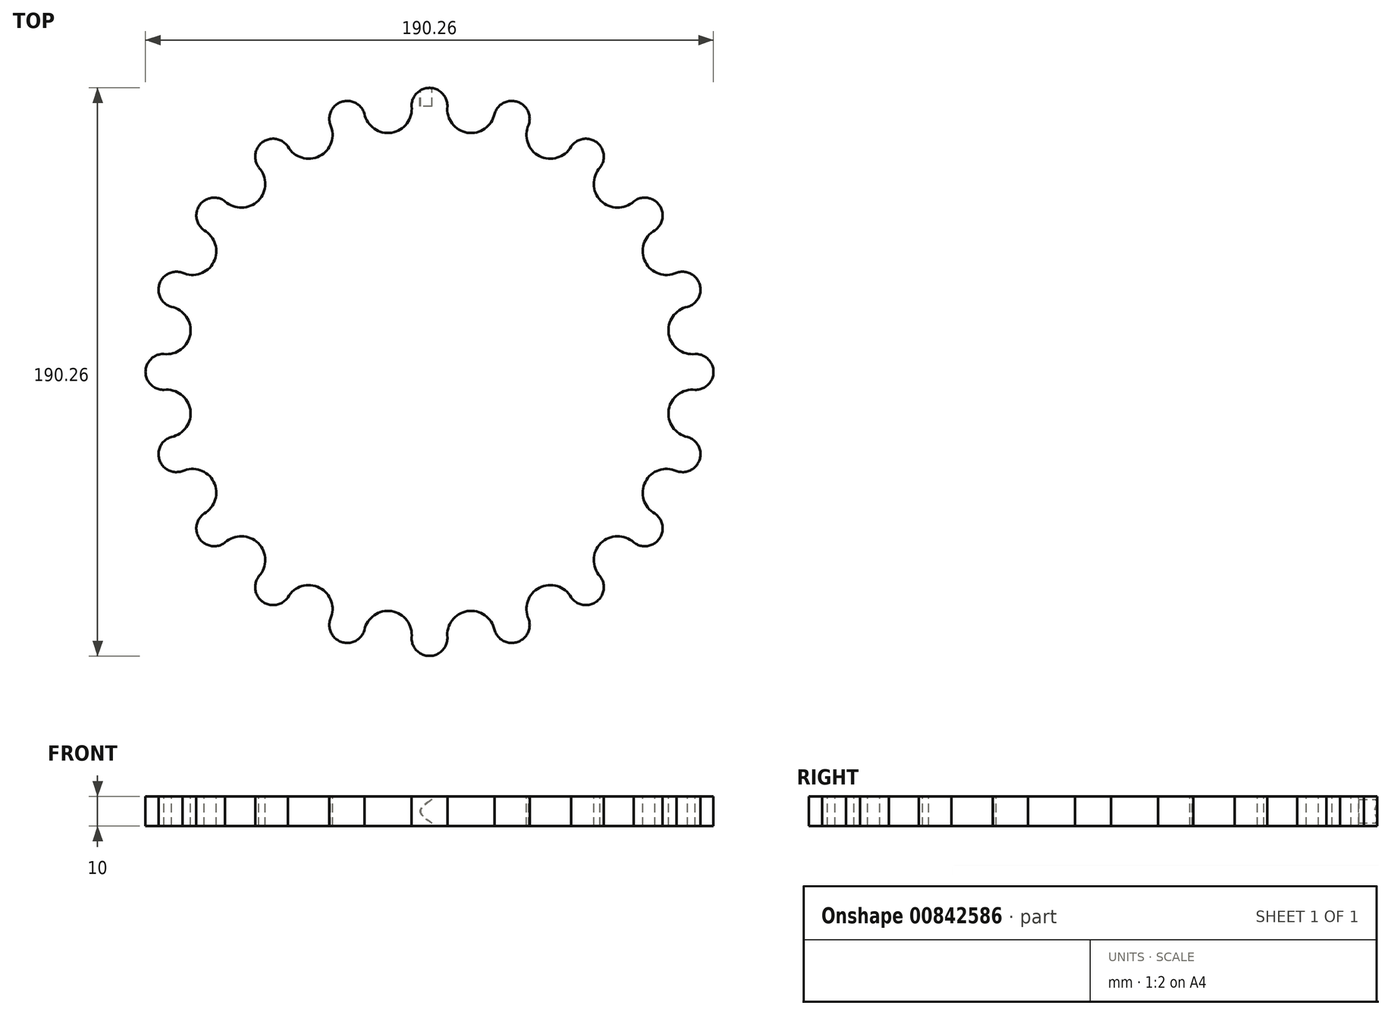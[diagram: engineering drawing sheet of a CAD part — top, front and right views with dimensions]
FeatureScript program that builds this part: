
annotation { "Feature Type Name" : "Feature", "Feature Type Description" : "" }
export const myFeature = defineFeature(function(context is Context, id is Id, definition is map)
    precondition{}
    {
        {
            var Q0;
            Q0=qCreatedBy(makeId("Top.planeOp"),FACE);
            var sketch = newSketch(context, id + "F0", { "sketchPlane" : qUnion([Q0])});
            skCircle(sketch, "E0", {"center": v(0, 0) * mm, "radius": 89.13 * mm});
            skCircle(sketch, "E1", {"center": v(0, 89.13) * mm, "radius": 7 * mm});
            skCircle(sketch, "E2.1.0", {"center": v(-13.94, 88.03) * mm, "radius": 7 * mm});
            skCircle(sketch, "E2.2.0", {"center": v(-27.54, 84.76) * mm, "radius": 7 * mm});
            skCircle(sketch, "E2.3.0", {"center": v(-40.46, 79.41) * mm, "radius": 7 * mm});
            skCircle(sketch, "E2.4.0", {"center": v(-52.39, 72.1) * mm, "radius": 7 * mm});
            skCircle(sketch, "E2.5.0", {"center": v(-63.02, 63.02) * mm, "radius": 7 * mm});
            skCircle(sketch, "E2.6.0", {"center": v(-72.1, 52.39) * mm, "radius": 7 * mm});
            skCircle(sketch, "E2.7.0", {"center": v(-79.41, 40.46) * mm, "radius": 7 * mm});
            skCircle(sketch, "E2.8.0", {"center": v(-84.76, 27.54) * mm, "radius": 7 * mm});
            skCircle(sketch, "E2.9.0", {"center": v(-88.03, 13.94) * mm, "radius": 7 * mm});
            skCircle(sketch, "E2.10.0", {"center": v(-89.13, 0) * mm, "radius": 7 * mm});
            skCircle(sketch, "E2.11.0", {"center": v(-88.03, -13.94) * mm, "radius": 7 * mm});
            skCircle(sketch, "E2.12.0", {"center": v(-84.76, -27.54) * mm, "radius": 7 * mm});
            skCircle(sketch, "E2.13.0", {"center": v(-79.41, -40.46) * mm, "radius": 7 * mm});
            skCircle(sketch, "E2.14.0", {"center": v(-72.1, -52.39) * mm, "radius": 7 * mm});
            skCircle(sketch, "E2.15.0", {"center": v(-63.02, -63.02) * mm, "radius": 7 * mm});
            skCircle(sketch, "E2.16.0", {"center": v(-52.39, -72.1) * mm, "radius": 7 * mm});
            skCircle(sketch, "E2.17.0", {"center": v(-40.46, -79.41) * mm, "radius": 7 * mm});
            skCircle(sketch, "E2.18.0", {"center": v(-27.54, -84.76) * mm, "radius": 7 * mm});
            skCircle(sketch, "E2.19.0", {"center": v(-13.94, -88.03) * mm, "radius": 7 * mm});
            skCircle(sketch, "E2.20.0", {"center": v(0, -89.13) * mm, "radius": 7 * mm});
            skCircle(sketch, "E2.21.0", {"center": v(13.94, -88.03) * mm, "radius": 7 * mm});
            skCircle(sketch, "E2.22.0", {"center": v(27.54, -84.76) * mm, "radius": 7 * mm});
            skCircle(sketch, "E2.23.0", {"center": v(40.46, -79.41) * mm, "radius": 7 * mm});
            skCircle(sketch, "E2.24.0", {"center": v(52.39, -72.1) * mm, "radius": 7 * mm});
            skCircle(sketch, "E2.25.0", {"center": v(63.02, -63.02) * mm, "radius": 7 * mm});
            skCircle(sketch, "E2.26.0", {"center": v(72.1, -52.39) * mm, "radius": 7 * mm});
            skCircle(sketch, "E2.27.0", {"center": v(79.41, -40.46) * mm, "radius": 7 * mm});
            skCircle(sketch, "E2.28.0", {"center": v(84.76, -27.54) * mm, "radius": 7 * mm});
            skCircle(sketch, "E2.29.0", {"center": v(88.03, -13.94) * mm, "radius": 7 * mm});
            skCircle(sketch, "E2.30.0", {"center": v(89.13, 0) * mm, "radius": 7 * mm});
            skCircle(sketch, "E2.31.0", {"center": v(88.03, 13.94) * mm, "radius": 7 * mm});
            skCircle(sketch, "E2.32.0", {"center": v(84.76, 27.54) * mm, "radius": 7 * mm});
            skCircle(sketch, "E2.33.0", {"center": v(79.41, 40.46) * mm, "radius": 7 * mm});
            skCircle(sketch, "E2.34.0", {"center": v(72.1, 52.39) * mm, "radius": 7 * mm});
            skCircle(sketch, "E2.35.0", {"center": v(63.02, 63.02) * mm, "radius": 7 * mm});
            skCircle(sketch, "E2.36.0", {"center": v(52.39, 72.1) * mm, "radius": 7 * mm});
            skCircle(sketch, "E2.37.0", {"center": v(40.46, 79.41) * mm, "radius": 7 * mm});
            skCircle(sketch, "E2.38.0", {"center": v(27.54, 84.76) * mm, "radius": 7 * mm});
            skCircle(sketch, "E2.39.0", {"center": v(13.94, 88.03) * mm, "radius": 7 * mm});
            skSolve(sketch);
        }
        {
            var Q0;
            {var subQ32=sQuery(id+"F0.wireOp",EDGE,"E2.1.0");var subQ34=sQuery(id+"F0.wireOp",EDGE,"E1");var subQ35=makeQuery(id+"F0.imprint","INTERSECT",VERTEX,{"disambiguationData":[OD(1.0)],"derivedFrom":[subQ34,subQ32]});Q0=makeQuery(id+"F0.imprint","IMPRINT",FACE,{"disambiguationData":[TD([[makeQuery(id+"F0.imprint","IMPRINT",EDGE,{"disambiguationData":[TD([[subQ35,-1.0]])],"derivedFrom":subQ34}),-1.0]])]});}
            var sketch = newSketch(context, id + "F1", { "sketchPlane" : qUnion([Q0])});
            skArc(sketch, "E3.0", {"start": v(-67.8, 57.91) * mm, "mid": v(-58.07, 58.07) * mm, "end": v(-57.91, 67.8) * mm});
            skArc(sketch, "E4.0.0", {"start": v(-57.91, 67.8) * mm, "mid": v(-57.9, 67.79) * mm, "end": v(-57.88, 67.77) * mm});
            skArc(sketch, "E4.0.2", {"start": v(-46.26, 75.49) * mm, "mid": v(-46.43, 75.76) * mm, "end": v(-46.6, 76.03) * mm});
            skArc(sketch, "E4.0.3", {"start": v(-46.6, 76.03) * mm, "mid": v(-56.5, 77.77) * mm, "end": v(-57.91, 67.8) * mm});
            skArc(sketch, "E5.0.0", {"start": v(-7, 88.85) * mm, "mid": v(-12.85, 81.12) * mm, "end": v(-20.8, 86.66) * mm});
            skArc(sketch, "E5.0.2", {"start": v(-34.1, 82.34) * mm, "mid": v(-37.02, 73.32) * mm, "end": v(-46.26, 75.49) * mm});
            skArc(sketch, "E5.0.4", {"start": v(-57.5, 67.32) * mm, "mid": v(-58.07, 58.07) * mm, "end": v(-67.32, 57.5) * mm});
            skArc(sketch, "E5.0.6", {"start": v(-75.49, 46.26) * mm, "mid": v(-73.32, 37.02) * mm, "end": v(-82.34, 34.1) * mm});
            skArc(sketch, "E5.0.8", {"start": v(-86.09, 20.67) * mm, "mid": v(-81.17, 12.56) * mm, "end": v(-88.85, 7) * mm});
            skArc(sketch, "E5.0.10", {"start": v(-88.85, -7) * mm, "mid": v(-81.12, -12.85) * mm, "end": v(-86.66, -20.8) * mm});
            skArc(sketch, "E5.0.12", {"start": v(-82.34, -34.1) * mm, "mid": v(-73.17, -37.3) * mm, "end": v(-76.03, -46.6) * mm});
            skArc(sketch, "E5.0.14", {"start": v(-67.77, -57.88) * mm, "mid": v(-58.07, -58.07) * mm, "end": v(-57.88, -67.77) * mm});
            skArc(sketch, "E5.0.16", {"start": v(-46.57, -76) * mm, "mid": v(-37.28, -73.18) * mm, "end": v(-34.1, -82.34) * mm});
            skArc(sketch, "E5.0.18", {"start": v(-20.8, -86.66) * mm, "mid": v(-12.85, -81.12) * mm, "end": v(-7, -88.85) * mm});
            skArc(sketch, "E5.0.20", {"start": v(7, -88.85) * mm, "mid": v(12.85, -81.12) * mm, "end": v(20.8, -86.66) * mm});
            skArc(sketch, "E5.0.22", {"start": v(34.12, -82.38) * mm, "mid": v(37.28, -73.18) * mm, "end": v(46.6, -76.03) * mm});
            skArc(sketch, "E5.0.24", {"start": v(57.88, -67.77) * mm, "mid": v(58.07, -58.07) * mm, "end": v(67.77, -57.88) * mm});
            skArc(sketch, "E5.0.26", {"start": v(76, -46.57) * mm, "mid": v(73.18, -37.28) * mm, "end": v(82.34, -34.1) * mm});
            skArc(sketch, "E5.0.28", {"start": v(86.66, -20.8) * mm, "mid": v(81.12, -12.85) * mm, "end": v(88.85, -7) * mm});
            skArc(sketch, "E5.0.30", {"start": v(88.85, 7) * mm, "mid": v(81.12, 12.85) * mm, "end": v(86.66, 20.8) * mm});
            skArc(sketch, "E5.0.32", {"start": v(82.34, 34.1) * mm, "mid": v(73.18, 37.28) * mm, "end": v(76, 46.57) * mm});
            skArc(sketch, "E5.0.34", {"start": v(67.77, 57.88) * mm, "mid": v(58.07, 58.07) * mm, "end": v(57.88, 67.77) * mm});
            skArc(sketch, "E5.0.36", {"start": v(46.57, 76) * mm, "mid": v(37.28, 73.18) * mm, "end": v(34.1, 82.34) * mm});
            skArc(sketch, "E5.0.38", {"start": v(20.8, 86.66) * mm, "mid": v(12.85, 81.12) * mm, "end": v(7, 88.85) * mm});
            skArc(sketch, "E6.0.0", {"start": v(-34.12, 82.38) * mm, "mid": v(-34.11, 82.36) * mm, "end": v(-34.1, 82.34) * mm});
            skArc(sketch, "E6.0.2", {"start": v(-20.8, 86.66) * mm, "mid": v(-20.81, 86.68) * mm, "end": v(-20.82, 86.7) * mm});
            skArc(sketch, "E6.0.3", {"start": v(-20.82, 86.7) * mm, "mid": v(-29.7, 91.42) * mm, "end": v(-34.12, 82.38) * mm});
            skArc(sketch, "E7.0.0", {"start": v(-7, 88.9) * mm, "mid": v(-7, 88.87) * mm, "end": v(-7, 88.85) * mm});
            skArc(sketch, "E7.0.2", {"start": v(7, 88.85) * mm, "mid": v(7, 88.87) * mm, "end": v(7, 88.9) * mm});
            skArc(sketch, "E7.0.3", {"start": v(7, 88.9) * mm, "mid": v(0, 96.13) * mm, "end": v(-7, 88.9) * mm});
            skArc(sketch, "E8.0.0", {"start": v(20.82, 86.7) * mm, "mid": v(20.81, 86.68) * mm, "end": v(20.8, 86.66) * mm});
            skArc(sketch, "E8.0.2", {"start": v(34.1, 82.34) * mm, "mid": v(34.11, 82.36) * mm, "end": v(34.12, 82.38) * mm});
            skArc(sketch, "E8.0.3", {"start": v(34.12, 82.38) * mm, "mid": v(29.7, 91.42) * mm, "end": v(20.82, 86.7) * mm});
            skArc(sketch, "E9.0.0", {"start": v(46.6, 76.03) * mm, "mid": v(46.58, 76.01) * mm, "end": v(46.57, 76) * mm});
            skArc(sketch, "E9.0.2", {"start": v(57.88, 67.77) * mm, "mid": v(57.9, 67.79) * mm, "end": v(57.91, 67.8) * mm});
            skArc(sketch, "E9.0.3", {"start": v(57.91, 67.8) * mm, "mid": v(56.5, 77.77) * mm, "end": v(46.6, 76.03) * mm});
            skArc(sketch, "E10.0.0", {"start": v(67.8, 57.91) * mm, "mid": v(67.79, 57.9) * mm, "end": v(67.77, 57.88) * mm});
            skArc(sketch, "E10.0.2", {"start": v(76, 46.57) * mm, "mid": v(76.01, 46.58) * mm, "end": v(76.03, 46.6) * mm});
            skArc(sketch, "E10.0.3", {"start": v(76.03, 46.6) * mm, "mid": v(77.77, 56.5) * mm, "end": v(67.8, 57.91) * mm});
            skArc(sketch, "E11.0.0", {"start": v(82.38, 34.12) * mm, "mid": v(82.36, 34.11) * mm, "end": v(82.34, 34.1) * mm});
            skArc(sketch, "E11.0.2", {"start": v(86.66, 20.8) * mm, "mid": v(86.68, 20.81) * mm, "end": v(86.7, 20.82) * mm});
            skArc(sketch, "E11.0.3", {"start": v(86.7, 20.82) * mm, "mid": v(91.42, 29.7) * mm, "end": v(82.38, 34.12) * mm});
            skArc(sketch, "E12.0.0", {"start": v(88.85, -7) * mm, "mid": v(88.87, -7) * mm, "end": v(88.9, -7) * mm});
            skArc(sketch, "E12.0.1", {"start": v(88.9, -7) * mm, "mid": v(96.13, 0) * mm, "end": v(88.9, 7) * mm});
            skArc(sketch, "E12.0.2", {"start": v(88.9, 7) * mm, "mid": v(88.87, 7) * mm, "end": v(88.85, 7) * mm});
            skArc(sketch, "E13.0.0", {"start": v(86.7, -20.82) * mm, "mid": v(86.68, -20.81) * mm, "end": v(86.66, -20.8) * mm});
            skArc(sketch, "E13.0.2", {"start": v(82.34, -34.1) * mm, "mid": v(82.36, -34.11) * mm, "end": v(82.38, -34.12) * mm});
            skArc(sketch, "E13.0.3", {"start": v(82.38, -34.12) * mm, "mid": v(91.42, -29.7) * mm, "end": v(86.7, -20.82) * mm});
            skArc(sketch, "E14.0.0", {"start": v(76.03, -46.6) * mm, "mid": v(76.01, -46.58) * mm, "end": v(76, -46.57) * mm});
            skArc(sketch, "E14.0.2", {"start": v(67.77, -57.88) * mm, "mid": v(67.79, -57.9) * mm, "end": v(67.8, -57.91) * mm});
            skArc(sketch, "E14.0.3", {"start": v(67.8, -57.91) * mm, "mid": v(77.77, -56.5) * mm, "end": v(76.03, -46.6) * mm});
            skArc(sketch, "E15.0.0", {"start": v(57.91, -67.8) * mm, "mid": v(57.9, -67.79) * mm, "end": v(57.88, -67.77) * mm});
            skArc(sketch, "E15.0.2", {"start": v(46.57, -76) * mm, "mid": v(46.58, -76.01) * mm, "end": v(46.6, -76.03) * mm});
            skArc(sketch, "E15.0.3", {"start": v(46.6, -76.03) * mm, "mid": v(56.5, -77.77) * mm, "end": v(57.91, -67.8) * mm});
            skArc(sketch, "E16.0.0", {"start": v(34.12, -82.38) * mm, "mid": v(34.11, -82.36) * mm, "end": v(34.1, -82.34) * mm});
            skArc(sketch, "E16.0.2", {"start": v(20.8, -86.66) * mm, "mid": v(20.81, -86.68) * mm, "end": v(20.82, -86.7) * mm});
            skArc(sketch, "E16.0.3", {"start": v(20.82, -86.7) * mm, "mid": v(29.7, -91.42) * mm, "end": v(34.12, -82.38) * mm});
            skArc(sketch, "E17.0.0", {"start": v(7, -88.9) * mm, "mid": v(7, -88.87) * mm, "end": v(7, -88.85) * mm});
            skArc(sketch, "E17.0.2", {"start": v(-7, -88.85) * mm, "mid": v(-7, -88.87) * mm, "end": v(-7, -88.9) * mm});
            skArc(sketch, "E17.0.3", {"start": v(-7, -88.9) * mm, "mid": v(0, -96.13) * mm, "end": v(7, -88.9) * mm});
            skArc(sketch, "E18.0.0", {"start": v(-20.82, -86.7) * mm, "mid": v(-20.81, -86.68) * mm, "end": v(-20.8, -86.66) * mm});
            skArc(sketch, "E18.0.2", {"start": v(-34.1, -82.34) * mm, "mid": v(-34.11, -82.36) * mm, "end": v(-34.12, -82.38) * mm});
            skArc(sketch, "E18.0.3", {"start": v(-34.12, -82.38) * mm, "mid": v(-29.7, -91.42) * mm, "end": v(-20.82, -86.7) * mm});
            skArc(sketch, "E19.0.0", {"start": v(-46.6, -76.03) * mm, "mid": v(-46.58, -76.01) * mm, "end": v(-46.57, -76) * mm});
            skArc(sketch, "E19.0.2", {"start": v(-57.88, -67.77) * mm, "mid": v(-57.9, -67.79) * mm, "end": v(-57.91, -67.8) * mm});
            skArc(sketch, "E19.0.3", {"start": v(-57.91, -67.8) * mm, "mid": v(-56.5, -77.77) * mm, "end": v(-46.6, -76.03) * mm});
            skArc(sketch, "E20.0.0", {"start": v(-67.8, -57.91) * mm, "mid": v(-67.79, -57.9) * mm, "end": v(-67.77, -57.88) * mm});
            skArc(sketch, "E20.0.2", {"start": v(-76, -46.57) * mm, "mid": v(-76.01, -46.58) * mm, "end": v(-76.03, -46.6) * mm});
            skArc(sketch, "E20.0.3", {"start": v(-76.03, -46.6) * mm, "mid": v(-77.77, -56.5) * mm, "end": v(-67.8, -57.91) * mm});
            skArc(sketch, "E21.0.0", {"start": v(-82.38, -34.12) * mm, "mid": v(-82.36, -34.11) * mm, "end": v(-82.34, -34.1) * mm});
            skArc(sketch, "E21.0.2", {"start": v(-86.66, -20.8) * mm, "mid": v(-86.68, -20.81) * mm, "end": v(-86.7, -20.82) * mm});
            skArc(sketch, "E21.0.3", {"start": v(-86.7, -20.82) * mm, "mid": v(-91.42, -29.7) * mm, "end": v(-82.38, -34.12) * mm});
            skArc(sketch, "E22.0.0", {"start": v(-88.9, -7) * mm, "mid": v(-88.87, -7) * mm, "end": v(-88.85, -7) * mm});
            skArc(sketch, "E22.0.2", {"start": v(-88.85, 7) * mm, "mid": v(-88.87, 7) * mm, "end": v(-88.9, 7) * mm});
            skArc(sketch, "E22.0.3", {"start": v(-88.9, 7) * mm, "mid": v(-96.13, 0) * mm, "end": v(-88.9, -7) * mm});
            skArc(sketch, "E23.0.0", {"start": v(-86.7, 20.82) * mm, "mid": v(-86.4, 20.75) * mm, "end": v(-86.09, 20.67) * mm});
            skArc(sketch, "E23.0.2", {"start": v(-82.34, 34.1) * mm, "mid": v(-82.36, 34.11) * mm, "end": v(-82.38, 34.12) * mm});
            skArc(sketch, "E23.0.3", {"start": v(-82.38, 34.12) * mm, "mid": v(-91.42, 29.7) * mm, "end": v(-86.7, 20.82) * mm});
            skArc(sketch, "E24.0.0", {"start": v(-76.03, 46.6) * mm, "mid": v(-75.76, 46.43) * mm, "end": v(-75.49, 46.26) * mm});
            skArc(sketch, "E24.0.2", {"start": v(-67.77, 57.88) * mm, "mid": v(-67.79, 57.9) * mm, "end": v(-67.8, 57.91) * mm});
            skArc(sketch, "E24.0.3", {"start": v(-67.8, 57.91) * mm, "mid": v(-77.77, 56.5) * mm, "end": v(-76.03, 46.6) * mm});
            skPoint(sketch, "E25.orphan", {"position": v(-86.66, 20.8) * mm});
            skPoint(sketch, "E26.orphan", {"position": v(-81.8, 33.88) * mm});
            skPoint(sketch, "E27.orphan", {"position": v(-76, 46.57) * mm});
            skPoint(sketch, "E28.orphan", {"position": v(-46.57, 76) * mm});
            skPoint(sketch, "E29.orphan", {"position": v(-33.88, 81.8) * mm});
            skPoint(sketch, "E30.orphan", {"position": v(-20.67, 86.09) * mm});
            skPoint(sketch, "E31.orphan", {"position": v(-6.95, 88.26) * mm});
            skPoint(sketch, "E32.orphan", {"position": v(6.95, 88.26) * mm});
            skPoint(sketch, "E33.orphan", {"position": v(20.67, 86.09) * mm});
            skPoint(sketch, "E34.orphan", {"position": v(33.88, 81.8) * mm});
            skPoint(sketch, "E35.orphan", {"position": v(46.26, 75.49) * mm});
            skPoint(sketch, "E36.orphan", {"position": v(57.5, 67.32) * mm});
            skPoint(sketch, "E37.orphan", {"position": v(67.32, 57.5) * mm});
            skPoint(sketch, "E38.orphan", {"position": v(75.49, 46.26) * mm});
            skPoint(sketch, "E39.orphan", {"position": v(81.8, 33.88) * mm});
            skPoint(sketch, "E40.orphan", {"position": v(86.09, 20.67) * mm});
            skPoint(sketch, "E41.orphan", {"position": v(88.26, 6.95) * mm});
            skPoint(sketch, "E42.orphan", {"position": v(88.26, -6.95) * mm});
            skPoint(sketch, "E43.orphan", {"position": v(86.09, -20.67) * mm});
            skPoint(sketch, "E44.orphan", {"position": v(81.8, -33.88) * mm});
            skPoint(sketch, "E45.orphan", {"position": v(75.49, -46.26) * mm});
            skPoint(sketch, "E46.orphan", {"position": v(67.32, -57.5) * mm});
            skPoint(sketch, "E47.orphan", {"position": v(57.5, -67.32) * mm});
            skPoint(sketch, "E48.orphan", {"position": v(46.26, -75.49) * mm});
            skPoint(sketch, "E49.orphan", {"position": v(33.88, -81.8) * mm});
            skPoint(sketch, "E50.orphan", {"position": v(20.67, -86.09) * mm});
            skPoint(sketch, "E51.orphan", {"position": v(6.95, -88.26) * mm});
            skPoint(sketch, "E52.orphan", {"position": v(-6.95, -88.26) * mm});
            skPoint(sketch, "E53.orphan", {"position": v(-20.67, -86.09) * mm});
            skPoint(sketch, "E54.orphan", {"position": v(-33.88, -81.8) * mm});
            skPoint(sketch, "E55.orphan", {"position": v(-46.26, -75.49) * mm});
            skPoint(sketch, "E56.orphan", {"position": v(-57.5, -67.32) * mm});
            skPoint(sketch, "E57.orphan", {"position": v(-67.32, -57.5) * mm});
            skPoint(sketch, "E58.orphan", {"position": v(-75.49, -46.26) * mm});
            skPoint(sketch, "E59.orphan", {"position": v(-81.8, -33.88) * mm});
            skPoint(sketch, "E60.orphan", {"position": v(-86.09, -20.67) * mm});
            skPoint(sketch, "E61.orphan", {"position": v(-88.26, -6.95) * mm});
            skPoint(sketch, "E62.orphan", {"position": v(-88.26, 6.95) * mm});
            skSolve(sketch);
        }
        {
            var Q0;
            Q0 = qSketchRegion(id + "F1", true);
            extrude(context, id + "F2", {"entities" : qUnion([Q0]), "depth" : 10 * mm, "offsetDistance" : 25 * mm});
        }
        {
            var Q0;
            Q0=makeQuery(id+"F2.opExtrude","CAP_FACE",FACE,{"disambiguationData":[OSD([sQuery(id+"F1.wireOp",EDGE,"E3.0"),sQuery(id+"F1.wireOp",EDGE,"E4.0.0"),sQuery(id+"F1.wireOp",EDGE,"E4.0.2"),sQuery(id+"F1.wireOp",EDGE,"E4.0.3"),sQuery(id+"F1.wireOp",EDGE,"E5.0.0"),sQuery(id+"F1.wireOp",EDGE,"E5.0.2"),sQuery(id+"F1.wireOp",EDGE,"E5.0.4"),sQuery(id+"F1.wireOp",EDGE,"E5.0.6"),sQuery(id+"F1.wireOp",EDGE,"E5.0.8"),sQuery(id+"F1.wireOp",EDGE,"E5.0.10"),sQuery(id+"F1.wireOp",EDGE,"E5.0.12"),sQuery(id+"F1.wireOp",EDGE,"E5.0.14"),sQuery(id+"F1.wireOp",EDGE,"E5.0.16"),sQuery(id+"F1.wireOp",EDGE,"E5.0.18"),sQuery(id+"F1.wireOp",EDGE,"E5.0.20"),sQuery(id+"F1.wireOp",EDGE,"E5.0.22"),sQuery(id+"F1.wireOp",EDGE,"E5.0.24"),sQuery(id+"F1.wireOp",EDGE,"E5.0.26"),sQuery(id+"F1.wireOp",EDGE,"E5.0.28"),sQuery(id+"F1.wireOp",EDGE,"E5.0.30"),sQuery(id+"F1.wireOp",EDGE,"E5.0.32"),sQuery(id+"F1.wireOp",EDGE,"E5.0.34"),sQuery(id+"F1.wireOp",EDGE,"E5.0.36"),sQuery(id+"F1.wireOp",EDGE,"E5.0.38"),sQuery(id+"F1.wireOp",EDGE,"E6.0.0"),sQuery(id+"F1.wireOp",EDGE,"E6.0.2"),sQuery(id+"F1.wireOp",EDGE,"E6.0.3"),sQuery(id+"F1.wireOp",EDGE,"E7.0.0"),sQuery(id+"F1.wireOp",EDGE,"E7.0.2"),sQuery(id+"F1.wireOp",EDGE,"E7.0.3"),sQuery(id+"F1.wireOp",EDGE,"E8.0.0"),sQuery(id+"F1.wireOp",EDGE,"E8.0.2"),sQuery(id+"F1.wireOp",EDGE,"E8.0.3"),sQuery(id+"F1.wireOp",EDGE,"E9.0.0"),sQuery(id+"F1.wireOp",EDGE,"E9.0.2"),sQuery(id+"F1.wireOp",EDGE,"E9.0.3"),sQuery(id+"F1.wireOp",EDGE,"E10.0.0"),sQuery(id+"F1.wireOp",EDGE,"E10.0.2"),sQuery(id+"F1.wireOp",EDGE,"E10.0.3"),sQuery(id+"F1.wireOp",EDGE,"E11.0.0"),sQuery(id+"F1.wireOp",EDGE,"E11.0.2"),sQuery(id+"F1.wireOp",EDGE,"E11.0.3"),sQuery(id+"F1.wireOp",EDGE,"E12.0.0"),sQuery(id+"F1.wireOp",EDGE,"E12.0.1"),sQuery(id+"F1.wireOp",EDGE,"E12.0.2"),sQuery(id+"F1.wireOp",EDGE,"E13.0.0"),sQuery(id+"F1.wireOp",EDGE,"E13.0.2"),sQuery(id+"F1.wireOp",EDGE,"E13.0.3"),sQuery(id+"F1.wireOp",EDGE,"E14.0.0"),sQuery(id+"F1.wireOp",EDGE,"E14.0.2"),sQuery(id+"F1.wireOp",EDGE,"E14.0.3"),sQuery(id+"F1.wireOp",EDGE,"E15.0.0"),sQuery(id+"F1.wireOp",EDGE,"E15.0.2"),sQuery(id+"F1.wireOp",EDGE,"E15.0.3"),sQuery(id+"F1.wireOp",EDGE,"E16.0.0"),sQuery(id+"F1.wireOp",EDGE,"E16.0.2"),sQuery(id+"F1.wireOp",EDGE,"E16.0.3"),sQuery(id+"F1.wireOp",EDGE,"E17.0.0"),sQuery(id+"F1.wireOp",EDGE,"E17.0.2"),sQuery(id+"F1.wireOp",EDGE,"E17.0.3"),sQuery(id+"F1.wireOp",EDGE,"E18.0.0"),sQuery(id+"F1.wireOp",EDGE,"E18.0.2"),sQuery(id+"F1.wireOp",EDGE,"E18.0.3"),sQuery(id+"F1.wireOp",EDGE,"E19.0.0"),sQuery(id+"F1.wireOp",EDGE,"E19.0.2"),sQuery(id+"F1.wireOp",EDGE,"E19.0.3"),sQuery(id+"F1.wireOp",EDGE,"E20.0.0"),sQuery(id+"F1.wireOp",EDGE,"E20.0.2"),sQuery(id+"F1.wireOp",EDGE,"E20.0.3"),sQuery(id+"F1.wireOp",EDGE,"E21.0.0"),sQuery(id+"F1.wireOp",EDGE,"E21.0.2"),sQuery(id+"F1.wireOp",EDGE,"E21.0.3"),sQuery(id+"F1.wireOp",EDGE,"E22.0.0"),sQuery(id+"F1.wireOp",EDGE,"E22.0.2"),sQuery(id+"F1.wireOp",EDGE,"E22.0.3"),sQuery(id+"F1.wireOp",EDGE,"E23.0.0"),sQuery(id+"F1.wireOp",EDGE,"E23.0.2"),sQuery(id+"F1.wireOp",EDGE,"E23.0.3"),sQuery(id+"F1.wireOp",EDGE,"E24.0.0"),sQuery(id+"F1.wireOp",EDGE,"E24.0.2"),sQuery(id+"F1.wireOp",EDGE,"E24.0.3")])],"isStart":false});
            var sketch = newSketch(context, id + "F3", { "sketchPlane" : qUnion([Q0])});
            skArc(sketch, "E63.0.0", {"start": v(-67.8, 57.91) * mm, "mid": v(-77.77, 56.5) * mm, "end": v(-76.03, 46.6) * mm});
            skArc(sketch, "E63.0.1", {"start": v(-76.03, 46.6) * mm, "mid": v(-73.18, 37.28) * mm, "end": v(-82.38, 34.12) * mm});
            skArc(sketch, "E63.0.2", {"start": v(-82.38, 34.12) * mm, "mid": v(-91.42, 29.7) * mm, "end": v(-86.7, 20.82) * mm});
            skArc(sketch, "E63.0.3", {"start": v(-86.7, 20.82) * mm, "mid": v(-81.12, 12.85) * mm, "end": v(-88.9, 7) * mm});
            skArc(sketch, "E63.0.4", {"start": v(-88.9, 7) * mm, "mid": v(-96.13, 0) * mm, "end": v(-88.9, -7) * mm});
            skArc(sketch, "E63.0.5", {"start": v(-88.9, -7) * mm, "mid": v(-81.12, -12.85) * mm, "end": v(-86.7, -20.82) * mm});
            skArc(sketch, "E63.0.6", {"start": v(-86.7, -20.82) * mm, "mid": v(-91.42, -29.7) * mm, "end": v(-82.38, -34.12) * mm});
            skArc(sketch, "E63.0.7", {"start": v(-82.38, -34.12) * mm, "mid": v(-73.18, -37.28) * mm, "end": v(-76.03, -46.6) * mm});
            skArc(sketch, "E63.0.8", {"start": v(-76.03, -46.6) * mm, "mid": v(-77.77, -56.5) * mm, "end": v(-67.8, -57.91) * mm});
            skArc(sketch, "E63.0.9", {"start": v(-67.8, -57.91) * mm, "mid": v(-58.07, -58.07) * mm, "end": v(-57.91, -67.8) * mm});
            skArc(sketch, "E63.0.10", {"start": v(-57.91, -67.8) * mm, "mid": v(-56.5, -77.77) * mm, "end": v(-46.6, -76.03) * mm});
            skArc(sketch, "E63.0.11", {"start": v(-46.6, -76.03) * mm, "mid": v(-37.28, -73.18) * mm, "end": v(-34.12, -82.38) * mm});
            skArc(sketch, "E63.0.12", {"start": v(-34.12, -82.38) * mm, "mid": v(-29.7, -91.42) * mm, "end": v(-20.82, -86.7) * mm});
            skArc(sketch, "E63.0.13", {"start": v(-20.82, -86.7) * mm, "mid": v(-12.85, -81.12) * mm, "end": v(-7, -88.9) * mm});
            skArc(sketch, "E63.0.14", {"start": v(-7, -88.9) * mm, "mid": v(0, -96.13) * mm, "end": v(7, -88.9) * mm});
            skArc(sketch, "E63.0.15", {"start": v(7, -88.9) * mm, "mid": v(12.85, -81.12) * mm, "end": v(20.82, -86.7) * mm});
            skArc(sketch, "E63.0.16", {"start": v(20.82, -86.7) * mm, "mid": v(29.7, -91.42) * mm, "end": v(34.12, -82.38) * mm});
            skArc(sketch, "E63.0.17", {"start": v(34.12, -82.38) * mm, "mid": v(37.28, -73.18) * mm, "end": v(46.6, -76.03) * mm});
            skArc(sketch, "E63.0.18", {"start": v(46.6, -76.03) * mm, "mid": v(56.5, -77.77) * mm, "end": v(57.91, -67.8) * mm});
            skArc(sketch, "E63.0.19", {"start": v(57.91, -67.8) * mm, "mid": v(58.07, -58.07) * mm, "end": v(67.8, -57.91) * mm});
            skArc(sketch, "E63.0.20", {"start": v(67.8, -57.91) * mm, "mid": v(77.77, -56.5) * mm, "end": v(76.03, -46.6) * mm});
            skArc(sketch, "E63.0.21", {"start": v(76.03, -46.6) * mm, "mid": v(73.18, -37.28) * mm, "end": v(82.38, -34.12) * mm});
            skArc(sketch, "E63.0.22", {"start": v(82.38, -34.12) * mm, "mid": v(91.42, -29.7) * mm, "end": v(86.7, -20.82) * mm});
            skArc(sketch, "E63.0.23", {"start": v(86.7, -20.82) * mm, "mid": v(81.12, -12.85) * mm, "end": v(88.9, -7) * mm});
            skArc(sketch, "E63.0.24", {"start": v(88.9, -7) * mm, "mid": v(96.13, 0) * mm, "end": v(88.9, 7) * mm});
            skArc(sketch, "E63.0.25", {"start": v(88.9, 7) * mm, "mid": v(81.12, 12.85) * mm, "end": v(86.7, 20.82) * mm});
            skArc(sketch, "E63.0.26", {"start": v(86.7, 20.82) * mm, "mid": v(91.42, 29.7) * mm, "end": v(82.38, 34.12) * mm});
            skArc(sketch, "E63.0.27", {"start": v(82.38, 34.12) * mm, "mid": v(73.18, 37.28) * mm, "end": v(76.03, 46.6) * mm});
            skArc(sketch, "E63.0.28", {"start": v(76.03, 46.6) * mm, "mid": v(77.77, 56.5) * mm, "end": v(67.8, 57.91) * mm});
            skArc(sketch, "E63.0.29", {"start": v(67.8, 57.91) * mm, "mid": v(58.07, 58.07) * mm, "end": v(57.91, 67.8) * mm});
            skArc(sketch, "E63.0.30", {"start": v(57.91, 67.8) * mm, "mid": v(56.5, 77.77) * mm, "end": v(46.6, 76.03) * mm});
            skArc(sketch, "E63.0.31", {"start": v(46.6, 76.03) * mm, "mid": v(37.28, 73.18) * mm, "end": v(34.12, 82.38) * mm});
            skArc(sketch, "E63.0.32", {"start": v(34.12, 82.38) * mm, "mid": v(29.7, 91.42) * mm, "end": v(20.82, 86.7) * mm});
            skArc(sketch, "E63.0.33", {"start": v(20.82, 86.7) * mm, "mid": v(12.85, 81.12) * mm, "end": v(7, 88.9) * mm});
            skArc(sketch, "E63.0.34", {"start": v(7, 88.9) * mm, "mid": v(0, 96.13) * mm, "end": v(-7, 88.9) * mm});
            skArc(sketch, "E63.0.35", {"start": v(-7, 88.9) * mm, "mid": v(-12.85, 81.12) * mm, "end": v(-20.82, 86.7) * mm});
            skArc(sketch, "E63.0.36", {"start": v(-20.82, 86.7) * mm, "mid": v(-29.7, 91.42) * mm, "end": v(-34.12, 82.38) * mm});
            skArc(sketch, "E63.0.37", {"start": v(-34.12, 82.38) * mm, "mid": v(-37.28, 73.18) * mm, "end": v(-46.6, 76.03) * mm});
            skArc(sketch, "E63.0.38", {"start": v(-46.6, 76.03) * mm, "mid": v(-56.5, 77.77) * mm, "end": v(-57.91, 67.8) * mm});
            skArc(sketch, "E63.0.39", {"start": v(-57.91, 67.8) * mm, "mid": v(-58.07, 58.07) * mm, "end": v(-67.8, 57.91) * mm});
            skArc(sketch, "E64.0", {"start": v(-57.15, 68.45) * mm, "mid": v(-57.37, 57.37) * mm, "end": v(-68.45, 57.15) * mm});
            skArc(sketch, "E64.1", {"start": v(-47.44, 75.5) * mm, "mid": v(-55.91, 76.96) * mm, "end": v(-57.15, 68.45) * mm});
            skArc(sketch, "E64.2", {"start": v(-33.2, 82.76) * mm, "mid": v(-36.83, 72.28) * mm, "end": v(-47.44, 75.5) * mm});
            skArc(sketch, "E64.3", {"start": v(-21.79, 86.47) * mm, "mid": v(-29.4, 90.47) * mm, "end": v(-33.2, 82.76) * mm});
            skArc(sketch, "E64.4", {"start": v(-6, 88.97) * mm, "mid": v(-12.7, 80.13) * mm, "end": v(-21.79, 86.47) * mm});
            skArc(sketch, "E64.5", {"start": v(6, 88.97) * mm, "mid": v(0, 95.13) * mm, "end": v(-6, 88.97) * mm});
            skArc(sketch, "E64.6", {"start": v(21.79, 86.47) * mm, "mid": v(12.7, 80.13) * mm, "end": v(6, 88.97) * mm});
            skArc(sketch, "E64.7", {"start": v(33.2, 82.76) * mm, "mid": v(29.4, 90.47) * mm, "end": v(21.79, 86.47) * mm});
            skArc(sketch, "E64.8", {"start": v(47.44, 75.5) * mm, "mid": v(36.83, 72.28) * mm, "end": v(33.2, 82.76) * mm});
            skArc(sketch, "E64.9", {"start": v(57.15, 68.45) * mm, "mid": v(55.91, 76.96) * mm, "end": v(47.44, 75.5) * mm});
            skArc(sketch, "E64.10", {"start": v(68.45, 57.15) * mm, "mid": v(57.37, 57.37) * mm, "end": v(57.15, 68.45) * mm});
            skArc(sketch, "E64.11", {"start": v(-68.45, 57.15) * mm, "mid": v(-76.96, 55.91) * mm, "end": v(-75.5, 47.44) * mm});
            skArc(sketch, "E64.12", {"start": v(75.5, 47.44) * mm, "mid": v(76.96, 55.91) * mm, "end": v(68.45, 57.15) * mm});
            skArc(sketch, "E64.13", {"start": v(82.76, 33.2) * mm, "mid": v(72.28, 36.83) * mm, "end": v(75.5, 47.44) * mm});
            skArc(sketch, "E64.14", {"start": v(86.47, 21.79) * mm, "mid": v(90.47, 29.4) * mm, "end": v(82.76, 33.2) * mm});
            skArc(sketch, "E64.15", {"start": v(88.97, 6) * mm, "mid": v(80.13, 12.7) * mm, "end": v(86.47, 21.79) * mm});
            skArc(sketch, "E64.16", {"start": v(88.97, -6) * mm, "mid": v(95.13, 0) * mm, "end": v(88.97, 6) * mm});
            skArc(sketch, "E64.17", {"start": v(86.47, -21.79) * mm, "mid": v(80.13, -12.7) * mm, "end": v(88.97, -6) * mm});
            skArc(sketch, "E64.18", {"start": v(-57.15, -68.45) * mm, "mid": v(-55.91, -76.96) * mm, "end": v(-47.44, -75.5) * mm});
            skArc(sketch, "E64.19", {"start": v(-68.45, -57.15) * mm, "mid": v(-57.37, -57.37) * mm, "end": v(-57.15, -68.45) * mm});
            skArc(sketch, "E64.20", {"start": v(-75.5, -47.44) * mm, "mid": v(-76.96, -55.91) * mm, "end": v(-68.45, -57.15) * mm});
            skArc(sketch, "E64.21", {"start": v(-82.76, -33.2) * mm, "mid": v(-72.28, -36.83) * mm, "end": v(-75.5, -47.44) * mm});
            skArc(sketch, "E64.22", {"start": v(-86.47, -21.79) * mm, "mid": v(-90.47, -29.4) * mm, "end": v(-82.76, -33.2) * mm});
            skArc(sketch, "E64.23", {"start": v(-88.97, -6) * mm, "mid": v(-80.13, -12.7) * mm, "end": v(-86.47, -21.79) * mm});
            skArc(sketch, "E64.24", {"start": v(-75.5, 47.44) * mm, "mid": v(-72.28, 36.83) * mm, "end": v(-82.76, 33.2) * mm});
            skArc(sketch, "E64.25", {"start": v(-82.76, 33.2) * mm, "mid": v(-90.47, 29.4) * mm, "end": v(-86.47, 21.79) * mm});
            skArc(sketch, "E64.26", {"start": v(-86.47, 21.79) * mm, "mid": v(-80.13, 12.7) * mm, "end": v(-88.97, 6) * mm});
            skArc(sketch, "E64.27", {"start": v(-88.97, 6) * mm, "mid": v(-95.13, 0) * mm, "end": v(-88.97, -6) * mm});
            skArc(sketch, "E64.28", {"start": v(-47.44, -75.5) * mm, "mid": v(-36.83, -72.28) * mm, "end": v(-33.2, -82.76) * mm});
            skArc(sketch, "E64.29", {"start": v(-33.2, -82.76) * mm, "mid": v(-29.4, -90.47) * mm, "end": v(-21.79, -86.47) * mm});
            skArc(sketch, "E64.30", {"start": v(-21.79, -86.47) * mm, "mid": v(-12.7, -80.13) * mm, "end": v(-6, -88.97) * mm});
            skArc(sketch, "E64.31", {"start": v(-6, -88.97) * mm, "mid": v(0, -95.13) * mm, "end": v(6, -88.97) * mm});
            skArc(sketch, "E64.32", {"start": v(6, -88.97) * mm, "mid": v(12.7, -80.13) * mm, "end": v(21.79, -86.47) * mm});
            skArc(sketch, "E64.33", {"start": v(21.79, -86.47) * mm, "mid": v(29.4, -90.47) * mm, "end": v(33.2, -82.76) * mm});
            skArc(sketch, "E64.34", {"start": v(33.2, -82.76) * mm, "mid": v(36.83, -72.28) * mm, "end": v(47.44, -75.5) * mm});
            skArc(sketch, "E64.35", {"start": v(47.44, -75.5) * mm, "mid": v(55.91, -76.96) * mm, "end": v(57.15, -68.45) * mm});
            skArc(sketch, "E64.36", {"start": v(57.15, -68.45) * mm, "mid": v(57.37, -57.37) * mm, "end": v(68.45, -57.15) * mm});
            skArc(sketch, "E64.37", {"start": v(68.45, -57.15) * mm, "mid": v(76.96, -55.91) * mm, "end": v(75.5, -47.44) * mm});
            skArc(sketch, "E64.38", {"start": v(75.5, -47.44) * mm, "mid": v(72.28, -36.83) * mm, "end": v(82.76, -33.2) * mm});
            skArc(sketch, "E64.39", {"start": v(82.76, -33.2) * mm, "mid": v(90.47, -29.4) * mm, "end": v(86.47, -21.79) * mm});
            skSolve(sketch);
        }
        {
            var Q0;
            Q0=makeQuery(id+"F3.imprint","IMPRINT",FACE,{"disambiguationData":[TD([[makeQuery(id+"F3.imprint","IMPRINT",EDGE,{"derivedFrom":sQuery(id+"F3.wireOp",EDGE,"E64.0")}),1.0]])]});
            extrude(context, id + "F4", {"entities" : qUnion([Q0]), "operationType" : NewBodyOperationType.REMOVE, "endBound" : BoundingType.THROUGH_ALL, "oppositeDirection" : true, "depth" : 25 * mm, "offsetDistance" : 25 * mm});
        }
        {
            var Q0;
            Q0=makeQuery(id+"F2.opExtrude","CAP_FACE",FACE,{"disambiguationData":[OSD([sQuery(id+"F1.wireOp",EDGE,"E3.0"),sQuery(id+"F1.wireOp",EDGE,"E4.0.0"),sQuery(id+"F1.wireOp",EDGE,"E4.0.2"),sQuery(id+"F1.wireOp",EDGE,"E4.0.3"),sQuery(id+"F1.wireOp",EDGE,"E5.0.0"),sQuery(id+"F1.wireOp",EDGE,"E5.0.2"),sQuery(id+"F1.wireOp",EDGE,"E5.0.4"),sQuery(id+"F1.wireOp",EDGE,"E5.0.6"),sQuery(id+"F1.wireOp",EDGE,"E5.0.8"),sQuery(id+"F1.wireOp",EDGE,"E5.0.10"),sQuery(id+"F1.wireOp",EDGE,"E5.0.12"),sQuery(id+"F1.wireOp",EDGE,"E5.0.14"),sQuery(id+"F1.wireOp",EDGE,"E5.0.16"),sQuery(id+"F1.wireOp",EDGE,"E5.0.18"),sQuery(id+"F1.wireOp",EDGE,"E5.0.20"),sQuery(id+"F1.wireOp",EDGE,"E5.0.22"),sQuery(id+"F1.wireOp",EDGE,"E5.0.24"),sQuery(id+"F1.wireOp",EDGE,"E5.0.26"),sQuery(id+"F1.wireOp",EDGE,"E5.0.28"),sQuery(id+"F1.wireOp",EDGE,"E5.0.30"),sQuery(id+"F1.wireOp",EDGE,"E5.0.32"),sQuery(id+"F1.wireOp",EDGE,"E5.0.34"),sQuery(id+"F1.wireOp",EDGE,"E5.0.36"),sQuery(id+"F1.wireOp",EDGE,"E5.0.38"),sQuery(id+"F1.wireOp",EDGE,"E6.0.0"),sQuery(id+"F1.wireOp",EDGE,"E6.0.2"),sQuery(id+"F1.wireOp",EDGE,"E6.0.3"),sQuery(id+"F1.wireOp",EDGE,"E7.0.0"),sQuery(id+"F1.wireOp",EDGE,"E7.0.2"),sQuery(id+"F1.wireOp",EDGE,"E7.0.3"),sQuery(id+"F1.wireOp",EDGE,"E8.0.0"),sQuery(id+"F1.wireOp",EDGE,"E8.0.2"),sQuery(id+"F1.wireOp",EDGE,"E8.0.3"),sQuery(id+"F1.wireOp",EDGE,"E9.0.0"),sQuery(id+"F1.wireOp",EDGE,"E9.0.2"),sQuery(id+"F1.wireOp",EDGE,"E9.0.3"),sQuery(id+"F1.wireOp",EDGE,"E10.0.0"),sQuery(id+"F1.wireOp",EDGE,"E10.0.2"),sQuery(id+"F1.wireOp",EDGE,"E10.0.3"),sQuery(id+"F1.wireOp",EDGE,"E11.0.0"),sQuery(id+"F1.wireOp",EDGE,"E11.0.2"),sQuery(id+"F1.wireOp",EDGE,"E11.0.3"),sQuery(id+"F1.wireOp",EDGE,"E12.0.0"),sQuery(id+"F1.wireOp",EDGE,"E12.0.1"),sQuery(id+"F1.wireOp",EDGE,"E12.0.2"),sQuery(id+"F1.wireOp",EDGE,"E13.0.0"),sQuery(id+"F1.wireOp",EDGE,"E13.0.2"),sQuery(id+"F1.wireOp",EDGE,"E13.0.3"),sQuery(id+"F1.wireOp",EDGE,"E14.0.0"),sQuery(id+"F1.wireOp",EDGE,"E14.0.2"),sQuery(id+"F1.wireOp",EDGE,"E14.0.3"),sQuery(id+"F1.wireOp",EDGE,"E15.0.0"),sQuery(id+"F1.wireOp",EDGE,"E15.0.2"),sQuery(id+"F1.wireOp",EDGE,"E15.0.3"),sQuery(id+"F1.wireOp",EDGE,"E16.0.0"),sQuery(id+"F1.wireOp",EDGE,"E16.0.2"),sQuery(id+"F1.wireOp",EDGE,"E16.0.3"),sQuery(id+"F1.wireOp",EDGE,"E17.0.0"),sQuery(id+"F1.wireOp",EDGE,"E17.0.2"),sQuery(id+"F1.wireOp",EDGE,"E17.0.3"),sQuery(id+"F1.wireOp",EDGE,"E18.0.0"),sQuery(id+"F1.wireOp",EDGE,"E18.0.2"),sQuery(id+"F1.wireOp",EDGE,"E18.0.3"),sQuery(id+"F1.wireOp",EDGE,"E19.0.0"),sQuery(id+"F1.wireOp",EDGE,"E19.0.2"),sQuery(id+"F1.wireOp",EDGE,"E19.0.3"),sQuery(id+"F1.wireOp",EDGE,"E20.0.0"),sQuery(id+"F1.wireOp",EDGE,"E20.0.2"),sQuery(id+"F1.wireOp",EDGE,"E20.0.3"),sQuery(id+"F1.wireOp",EDGE,"E21.0.0"),sQuery(id+"F1.wireOp",EDGE,"E21.0.2"),sQuery(id+"F1.wireOp",EDGE,"E21.0.3"),sQuery(id+"F1.wireOp",EDGE,"E22.0.0"),sQuery(id+"F1.wireOp",EDGE,"E22.0.2"),sQuery(id+"F1.wireOp",EDGE,"E22.0.3"),sQuery(id+"F1.wireOp",EDGE,"E23.0.0"),sQuery(id+"F1.wireOp",EDGE,"E23.0.2"),sQuery(id+"F1.wireOp",EDGE,"E23.0.3"),sQuery(id+"F1.wireOp",EDGE,"E24.0.0"),sQuery(id+"F1.wireOp",EDGE,"E24.0.2"),sQuery(id+"F1.wireOp",EDGE,"E24.0.3")])],"isStart":false});
            var sketch = newSketch(context, id + "F5", { "sketchPlane" : qUnion([Q0])});
            skLineSegment(sketch, "E65.bottom", {"start": v(0, 99.51) * mm, "end": v(0, 99.51) * mm});
            skLineSegment(sketch, "E65.top", {"start": v(0, 85.69) * mm, "end": v(0, 85.69) * mm});
            skLineSegment(sketch, "E65.left", {"start": v(0, 99.51) * mm, "end": v(0, 85.69) * mm});
            skLineSegment(sketch, "E65.right", {"start": v(0, 99.51) * mm, "end": v(0, 85.69) * mm});
            skPoint(sketch, "E65.middle", {"position": v(0, 92.6) * mm});
            skPoint(sketch, "E65.middle.positionSnap0", {"position": v(0, 95.13) * mm});
            skPoint(sketch, "E65.centerSnap0", {"position": v(0, 95.13) * mm});
            skSolve(sketch);
        }
        {
            var Q0;
            Q0=qCreatedBy(makeId("Front.planeOp"),FACE);
            cPlane(context, id + "F6", {"entities" : qUnion([Q0]), "cplaneType" : CPlaneType.OFFSET, "offset" : 108.9 * mm, "oppositeDirection" : true, "width" : 150 * mm, "height" : 150 * mm});
        }
        {
            var Q0;
            Q0=qCreatedBy(id+"F6.planeOp",FACE);
            var sketch = newSketch(context, id + "F7", { "sketchPlane" : qUnion([Q0])});
            skLineSegment(sketch, "E66", {"start": v(0, 0) * mm, "end": v(0, 10) * mm, "construction": true});
            skLineSegment(sketch, "E67.0", {"start": v(3, 0) * mm, "end": v(3, 10.5) * mm, "construction": true});
            skLineSegment(sketch, "E68.0", {"start": v(-3, 0) * mm, "end": v(-3, 10) * mm, "construction": true});
            skLineSegment(sketch, "E69", {"start": v(3, 0) * mm, "end": v(3, -0.5) * mm, "construction": true});
            skFitSpline(sketch, "E70", {"points": [v(3, 10.5) * mm, v(-3, 5) * mm, v(3, -0.5) * mm], "startDerivative": vector(-18, -14) * mm, "endDerivative": vector(18, -14) * mm});
            skFitSpline(sketch, "E71.0", {"points": [v(3, 10.5) * mm, v(1.5, 9.34) * mm, v(-0.76, 7.87) * mm, v(-2.63, 6.2) * mm, v(-3.2, 5) * mm, v(-2.63, 3.8) * mm, v(-0.76, 2.13) * mm, v(1.5, 0.66) * mm, v(3, -0.5) * mm]});
            skLineSegment(sketch, "E72", {"start": v(3, 10.5) * mm, "end": v(3, 10.5) * mm});
            skLineSegment(sketch, "E73", {"start": v(3, -0.5) * mm, "end": v(3, -0.5) * mm});
            skSolve(sketch);
        }
        {
            var Q0;
            Q0=makeQuery(id+"F7.imprint","IMPRINT",FACE,{"disambiguationData":[TD([[makeQuery(id+"F7.imprint","IMPRINT",EDGE,{"derivedFrom":sQuery(id+"F7.wireOp",EDGE,"E70")}),-1.0]])]});
            extrude(context, id + "F8", {"entities" : qUnion([Q0]), "operationType" : NewBodyOperationType.REMOVE, "depth" : 20 * mm, "offsetDistance" : 25 * mm});
        }
    });
